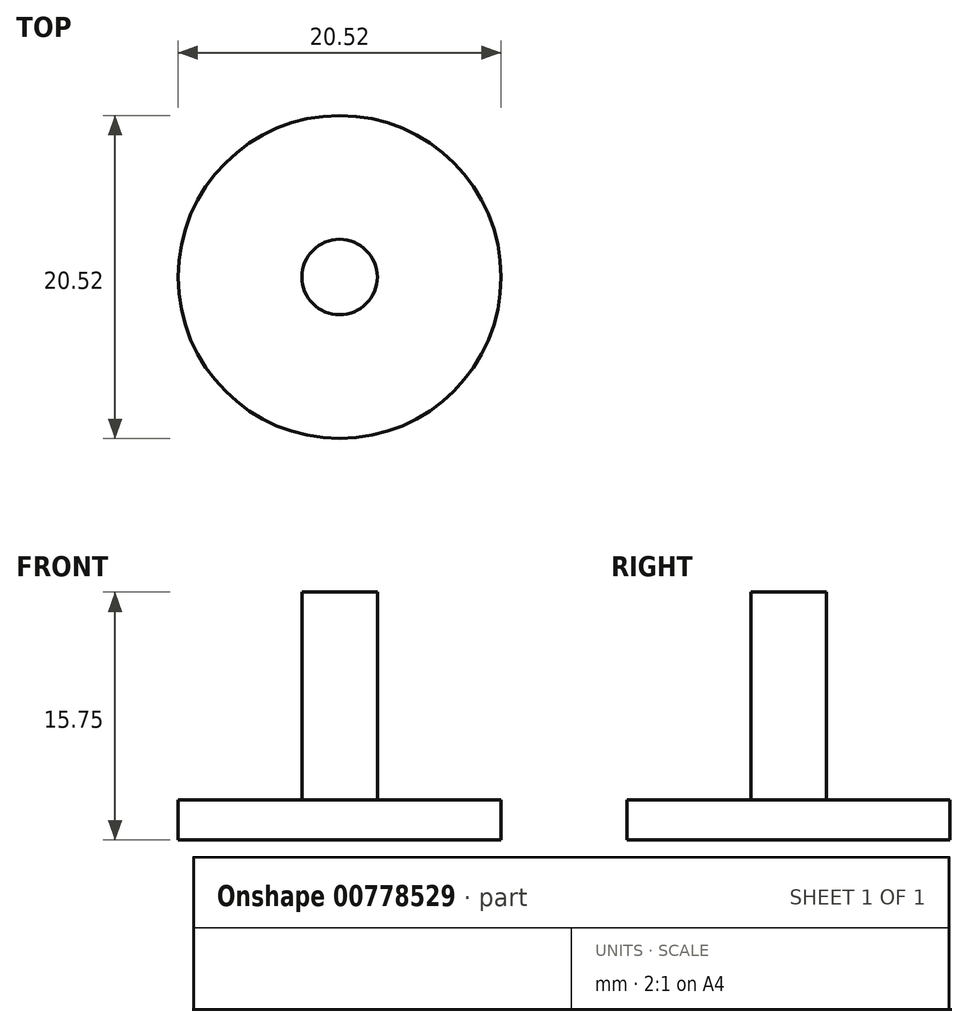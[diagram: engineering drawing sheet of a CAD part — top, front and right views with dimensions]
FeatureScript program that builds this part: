
annotation { "Feature Type Name" : "Feature", "Feature Type Description" : "" }
export const myFeature = defineFeature(function(context is Context, id is Id, definition is map)
    precondition{}
    {
        {
            var Q0;
            Q0=qCreatedBy(makeId("Top.planeOp"),FACE);
            var sketch = newSketch(context, id + "F0", { "sketchPlane" : qUnion([Q0])});
            skCircle(sketch, "E0", {"center": v(0, 0) * mm, "radius": 10.26 * mm});
            skSolve(sketch);
        }
        {
            var Q0;
            Q0=qCreatedBy(makeId("Top.planeOp"),FACE);
            var sketch = newSketch(context, id + "F1", { "sketchPlane" : qUnion([Q0])});
            skCircle(sketch, "E1", {"center": v(0, 0) * mm, "radius": 2.4 * mm});
            skSolve(sketch);
        }
        {
            var Q0;
            Q0 = qSketchRegion(id + "F0", true);
            extrude(context, id + "F2", {"entities" : qUnion([Q0]), "depth" : 2.54 * mm, "offsetDistance" : 25.4 * mm});
        }
        {
            var Q0;
            Q0 = qSketchRegion(id + "F1", true);
            extrude(context, id + "F3", {"entities" : qUnion([Q0]), "operationType" : NewBodyOperationType.ADD, "depth" : 15.75 * mm, "offsetDistance" : 25.4 * mm});
        }
    });
